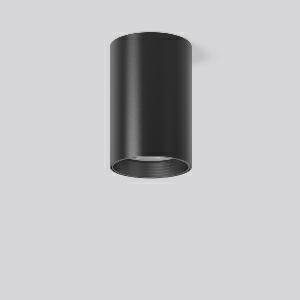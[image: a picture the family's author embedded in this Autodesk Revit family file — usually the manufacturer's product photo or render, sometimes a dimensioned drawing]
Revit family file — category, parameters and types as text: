
# Revit family: heledon_maxi_a_931241_003_f203
name_source: partatom
category: Lighting Fixtures
units: mm (PartAtom-declared; Revit-internal decimal feet)

## family parameters
Cut with Voids When Loaded = No
Host = Face
Light Source = No
Part Type = Normal
Room Calculation Point = No
Round Connector Dimension = Use Diameter
Shared = No

## types (1)
- HELEDON maxi A (1 x LED Modul 920 meat+, 1900 lm, 2000)
    Apparent Load = 33 VA
    Approval mark = CE
    CIE Flux Codes = 97 100 100 100 100
    Color Rendering = 90
    Color Temperature = 2000
    Default Elevation = 1800 mm
    Description = Series: HELEDON maxi
Cylindrical surface-mounted downlight. Housing: die-cast aluminium, powder-coated. Internal ceiling frame polycarbonate with bayonet mounting. Black plastic ring and recessed LED to prevent glare from the side. Optical assembly with lens made of plastic (polycarbonate) for the best homogeneous light distribution - can be changed without tools. Special LED for illumination of meat included. Suitable for Ceiling mounting. Easy installation with a separate ceiling frame with bayonet mounting and plug connection. Driver integrated. Connected via plug-in connector. High quality converter without flickering and stroboscopic effect. The following accessories can be mounted without use of tools: interchangeable lenses, decorative glasses, honeycomb louvre, clear and frosted diffusers, white interchangeable plastic ring. 
Colour: deep black, matt (RAL 9005)
Diameter: 123 mm
Height: 183 mm
Lamp: LED
Socket: without socket
Colour temperature: meat +
System power: 33 W
Rated luminous flux: 1900 lm
Luminous efficiency: 58 lm/W
Control gear: Regulated power supply
Protection class: I
Type of protection: IP 20
    Height = 183 mm
    Lamp = 1 x LED Modul 920 meat+
    Lamp Light Flux = 1900 lm
    Lamp count = 1
    Length = 123 mm
    Lifetime = 50000 h
    Luminous efficacy = 58 lm/W
    Manufacturer = RZB
    ModVariant = No
    Model = 931241.003
    Mounting Place = Ceiling
    Mounting Type = Surface mounted
    Number of Poles = 1
    OnlyDefault = Yes
    Power Factor = 1
    Product Name = HELEDON maxi A
    Product group = Surface mounted downlights
    ProductGroupID = 302
    Protection Class = Protection class I
    Protection Degree = IP 20
    RLX_Detail_Level = 1
    RLX_Emergency_Light_Flux = 0 lm
    RLX_Emergency_Type = 0
    RLX_Emergency_Type_DB = No
    RlxData = <blob elided: 97049 chars, md5=0e6aca8c>
    Socket = socket
    Standby Power = 0 W
    System Light Flux = 1900 lm
    System Power = 33 W
    Type Comments = Product without accessories
    Type Image = 931193.003.jpg
    URL = http://relux.com
    VarID = ---
    Voltage = 230 V
    Voltage Range = 220-240 V
    Weight = 0.00 kg
    Width = 0 mm  [stored 0 ft]

note: [stored X ft] marks values corroborated as IEEE doubles in the binary element streams (Revit-internal decimal feet)

## geometry (parser evidence)
native form markers: Blend x4, Sweep x10
no freeform markers — native parametric forms only
